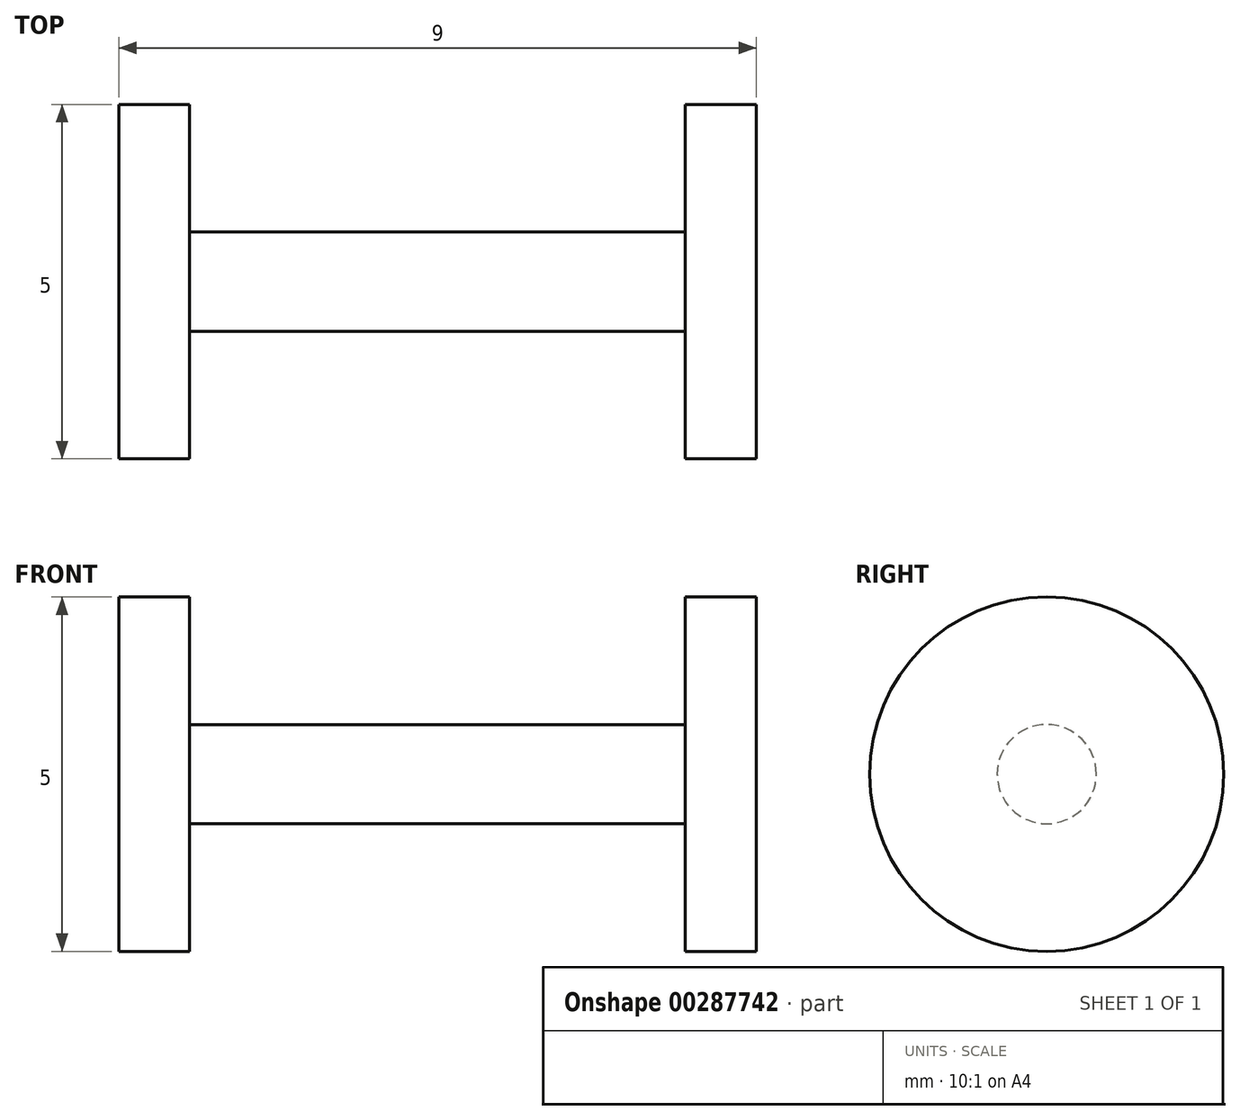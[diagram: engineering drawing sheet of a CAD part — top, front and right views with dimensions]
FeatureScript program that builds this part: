
annotation { "Feature Type Name" : "Feature", "Feature Type Description" : "" }
export const myFeature = defineFeature(function(context is Context, id is Id, definition is map)
    precondition{}
    {
        {
            var Q0;
            Q0=qCreatedBy(makeId("Front.planeOp"),FACE);
            var sketch = newSketch(context, id + "F0", { "sketchPlane" : qUnion([Q0])});
            skLineSegment(sketch, "E0", {"start": v(0, 8.37) * mm, "end": v(0, -9.23) * mm, "construction": true});
            skLineSegment(sketch, "E1", {"start": v(8.25, 0) * mm, "end": v(-8.12, 0) * mm, "construction": true});
            skLineSegment(sketch, "E2", {"start": v(0, 0.7) * mm, "end": v(3.5, 0.7) * mm});
            skLineSegment(sketch, "E3", {"start": v(3.5, 0.7) * mm, "end": v(3.5, 2.5) * mm});
            skLineSegment(sketch, "E4", {"start": v(3.5, 2.5) * mm, "end": v(4.5, 2.5) * mm});
            skLineSegment(sketch, "E5", {"start": v(4.5, 2.5) * mm, "end": v(4.5, 0) * mm});
            skLineSegment(sketch, "E6.MirrorCS", {"start": v(-3.5, 0.7) * mm, "end": v(-3.5, 2.5) * mm});
            skLineSegment(sketch, "E7.MirrorCS", {"start": v(-4.5, 2.5) * mm, "end": v(-4.5, 0) * mm});
            skLineSegment(sketch, "E8.MirrorCS", {"start": v(-3.5, 2.5) * mm, "end": v(-4.5, 2.5) * mm});
            skLineSegment(sketch, "E9.MirrorCS", {"start": v(0, 0.7) * mm, "end": v(-3.5, 0.7) * mm});
            skLineSegment(sketch, "E10", {"start": v(-4.5, 0) * mm, "end": v(4.5, 0) * mm});
            skSolve(sketch);
        }
        {
            var Q0;
            Q0 = qSketchRegion(id + "F0", true);
            var Q1;
            Q1=sQuery(id+"F0.wireOp",EDGE,"E1");
            revolve(context, id + "F1", {"entities" : qUnion([Q0]), "axis" : qUnion([Q1]), "revolveType" : RevolveType.FULL});
        }
        {
            var Q0;
            Q0=qCreatedBy(makeId("Right.planeOp"),FACE);
            cPlane(context, id + "F2", {"entities" : qUnion([Q0]), "cplaneType" : CPlaneType.OFFSET, "offset" : 2 * mm, "width" : 150 * mm, "height" : 150 * mm});
        }
        {
            var Q0;
            Q0=qCreatedBy(id+"F2.planeOp",FACE);
            var sketch = newSketch(context, id + "F3", { "sketchPlane" : qUnion([Q0])});
            skCircle(sketch, "E11.0", {"center": v(0, 0) * mm, "radius": 0.7 * mm});
            skSolve(sketch);
        }
    });
